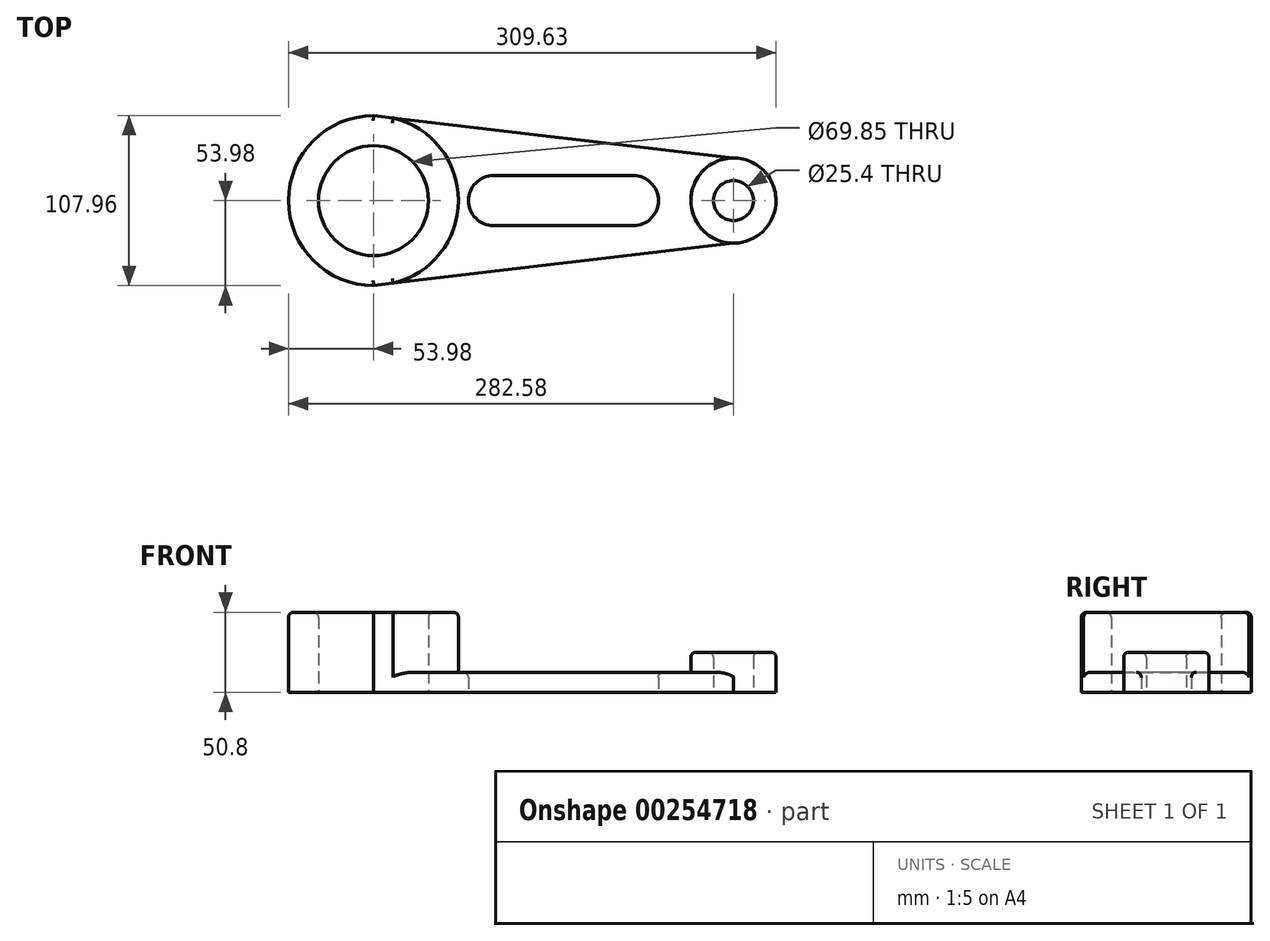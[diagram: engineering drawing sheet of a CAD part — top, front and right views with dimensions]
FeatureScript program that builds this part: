
annotation { "Feature Type Name" : "Feature", "Feature Type Description" : "" }
export const myFeature = defineFeature(function(context is Context, id is Id, definition is map)
    precondition{}
    {
        {
            var Q0;
            Q0=qCreatedBy(makeId("Top.planeOp"),FACE);
            var sketch = newSketch(context, id + "F0", { "sketchPlane" : qUnion([Q0])});
            skCircle(sketch, "E0", {"center": v(0, 0) * mm, "radius": 12.7 * mm});
            skCircle(sketch, "E1", {"center": v(0, 0) * mm, "radius": 27.05 * mm});
            skCircle(sketch, "E2", {"center": v(-228.6, 0) * mm, "radius": 34.93 * mm});
            skCircle(sketch, "E3", {"center": v(-228.6, 0) * mm, "radius": 53.98 * mm});
            skCircle(sketch, "E4", {"center": v(-152.4, 0) * mm, "radius": 15.88 * mm});
            skCircle(sketch, "E5", {"center": v(-63.5, 0) * mm, "radius": 15.88 * mm});
            skLineSegment(sketch, "E6", {"start": v(-152.4, 15.88) * mm, "end": v(-63.5, 15.88) * mm});
            skLineSegment(sketch, "E7", {"start": v(-152.4, -15.88) * mm, "end": v(-63.5, -15.88) * mm});
            skLineSegment(sketch, "E8", {"start": v(0, 27.05) * mm, "end": v(-228.6, 53.97) * mm});
            skLineSegment(sketch, "E9", {"start": v(-228.6, 0) * mm, "end": v(0, 0) * mm});
            skLineSegment(sketch, "E10.MirrorCS", {"start": v(0, -27.05) * mm, "end": v(-228.6, -53.98) * mm});
            skSolve(sketch);
        }
        {
            var Q0;
            {var subQ0=sQuery(id+"F0.wireOp",EDGE,"E6");Q0=makeQuery(id+"F0.imprint","IMPRINT",FACE,{"disambiguationData":[TD([[makeQuery(id+"F0.imprint","IMPRINT",EDGE,{"derivedFrom":subQ0}),1.0]])]});}
            var Q1;
            {var subQ0=sQuery(id+"F0.wireOp",EDGE,"E7");Q1=makeQuery(id+"F0.imprint","IMPRINT",FACE,{"disambiguationData":[TD([[makeQuery(id+"F0.imprint","IMPRINT",EDGE,{"derivedFrom":subQ0}),-1.0]])]});}
            extrude(context, id + "F1", {"entities" : qUnion([Q0, Q1]), "depth" : 12.7 * mm});
        }
        {
            var Q0;
            Q0=makeQuery(id+"F0.imprint","IMPRINT",FACE,{"disambiguationData":[TD([[makeQuery(id+"F0.imprint","IMPRINT",EDGE,{"derivedFrom":sQuery(id+"F0.wireOp",EDGE,"E2")}),-1.0]])]});
            extrude(context, id + "F2", {"entities" : qUnion([Q0]), "operationType" : NewBodyOperationType.ADD, "depth" : 50.8 * mm});
        }
        {
            var Q0;
            Q0=makeQuery(id+"F0.imprint","IMPRINT",FACE,{"disambiguationData":[TD([[makeQuery(id+"F0.imprint","IMPRINT",EDGE,{"derivedFrom":sQuery(id+"F0.wireOp",EDGE,"E0")}),-1.0]])]});
            extrude(context, id + "F3", {"entities" : qUnion([Q0]), "operationType" : NewBodyOperationType.ADD, "depth" : 25.4 * mm});
        }
        {
            var Q0;
            {var subQ0=sQuery(id+"F0.wireOp",EDGE,"E3");Q0=makeQuery(id+"F2.opExtrude","CAP_EDGE",EDGE,{"disambiguationData":[OSD([subQ0]),TDD([makeQuery(id+"F0.imprint","IMPRINT",EDGE,{"disambiguationData":[TD([[makeQuery(id+"F0.imprint","INTERSECT",VERTEX,{"disambiguationData":[OD(0.0)],"derivedFrom":[subQ0,sQuery(id+"F0.wireOp",EDGE,"E8")]}),-1.0]])],"derivedFrom":subQ0})])],"isStart":false});}
            var Q1;
            {var subQ0=sQuery(id+"F0.wireOp",EDGE,"E3");var subQ1=makeQuery(id+"F0.imprint","INTERSECT",VERTEX,{"derivedFrom":[subQ0,sQuery(id+"F0.wireOp",EDGE,"E9")]});Q1=makeQuery(id+"F2.opExtrude","CAP_EDGE",EDGE,{"disambiguationData":[OSD([subQ0]),TDD([makeQuery(id+"F0.imprint","IMPRINT",EDGE,{"disambiguationData":[TD([[makeQuery(id+"F0.imprint","INTERSECT",VERTEX,{"disambiguationData":[OD(1.0)],"derivedFrom":[subQ0,sQuery(id+"F0.wireOp",EDGE,"E8")]}),1.0]])],"derivedFrom":subQ0}),makeQuery(id+"F0.imprint","IMPRINT",EDGE,{"disambiguationData":[TD([[subQ1,1.0]])],"derivedFrom":subQ0})])],"isStart":false});}
            var Q2;
            Q2=makeQuery(id+"F1.opExtrude","CAP_EDGE",EDGE,{"disambiguationData":[OSD([sQuery(id+"F0.wireOp",EDGE,"E10.MirrorCS")])],"isStart":false});
            var Q3;
            Q3=makeQuery(id+"F1.opExtrude","CAP_EDGE",EDGE,{"disambiguationData":[OSD([sQuery(id+"F0.wireOp",EDGE,"E8")])],"isStart":false});
            var Q4;
            Q4=makeQuery(id+"F3.opExtrude","CAP_EDGE",EDGE,{"disambiguationData":[OSD([sQuery(id+"F0.wireOp",EDGE,"E1")])],"isStart":false});
            var Q5;
            Q5=makeQuery(id+"F2.opExtrude","CAP_EDGE",EDGE,{"disambiguationData":[OSD([sQuery(id+"F0.wireOp",EDGE,"E10.MirrorCS")])],"isStart":false});
            var Q6;
            Q6=makeQuery(id+"F2.opExtrude","CAP_EDGE",EDGE,{"disambiguationData":[OSD([sQuery(id+"F0.wireOp",EDGE,"E8")])],"isStart":false});
            var Q7;
            Q7=makeQuery(id+"F2.opExtrude","CAP_EDGE",EDGE,{"disambiguationData":[OSD([sQuery(id+"F0.wireOp",EDGE,"E2")])],"isStart":false});
            var Q8;
            Q8=makeQuery(id+"F1.opExtrude","CAP_EDGE",EDGE,{"disambiguationData":[OSD([sQuery(id+"F0.wireOp",EDGE,"E7")])],"isStart":false});
            var Q9;
            Q9=makeQuery(id+"F1.opExtrude","CAP_EDGE",EDGE,{"disambiguationData":[OSD([sQuery(id+"F0.wireOp",EDGE,"E4")])],"isStart":false});
            var Q10;
            Q10=makeQuery(id+"F1.opExtrude","CAP_EDGE",EDGE,{"disambiguationData":[OSD([sQuery(id+"F0.wireOp",EDGE,"E6")])],"isStart":false});
            var Q11;
            Q11=makeQuery(id+"F1.opExtrude","CAP_EDGE",EDGE,{"disambiguationData":[OSD([sQuery(id+"F0.wireOp",EDGE,"E5")])],"isStart":false});
            var Q12;
            Q12=makeQuery(id+"F3.opExtrude","CAP_EDGE",EDGE,{"disambiguationData":[OSD([sQuery(id+"F0.wireOp",EDGE,"E0")])],"isStart":false});
            fillet(context, id + "F4", {"entities" : qUnion([Q0, Q1, Q2, Q3, Q4, Q5, Q6, Q7, Q8, Q9, Q10, Q11, Q12]), "radius" : 3.17 * mm, "tangentPropagation" : true, "allowEdgeOverflow" : false});
        }
    });
